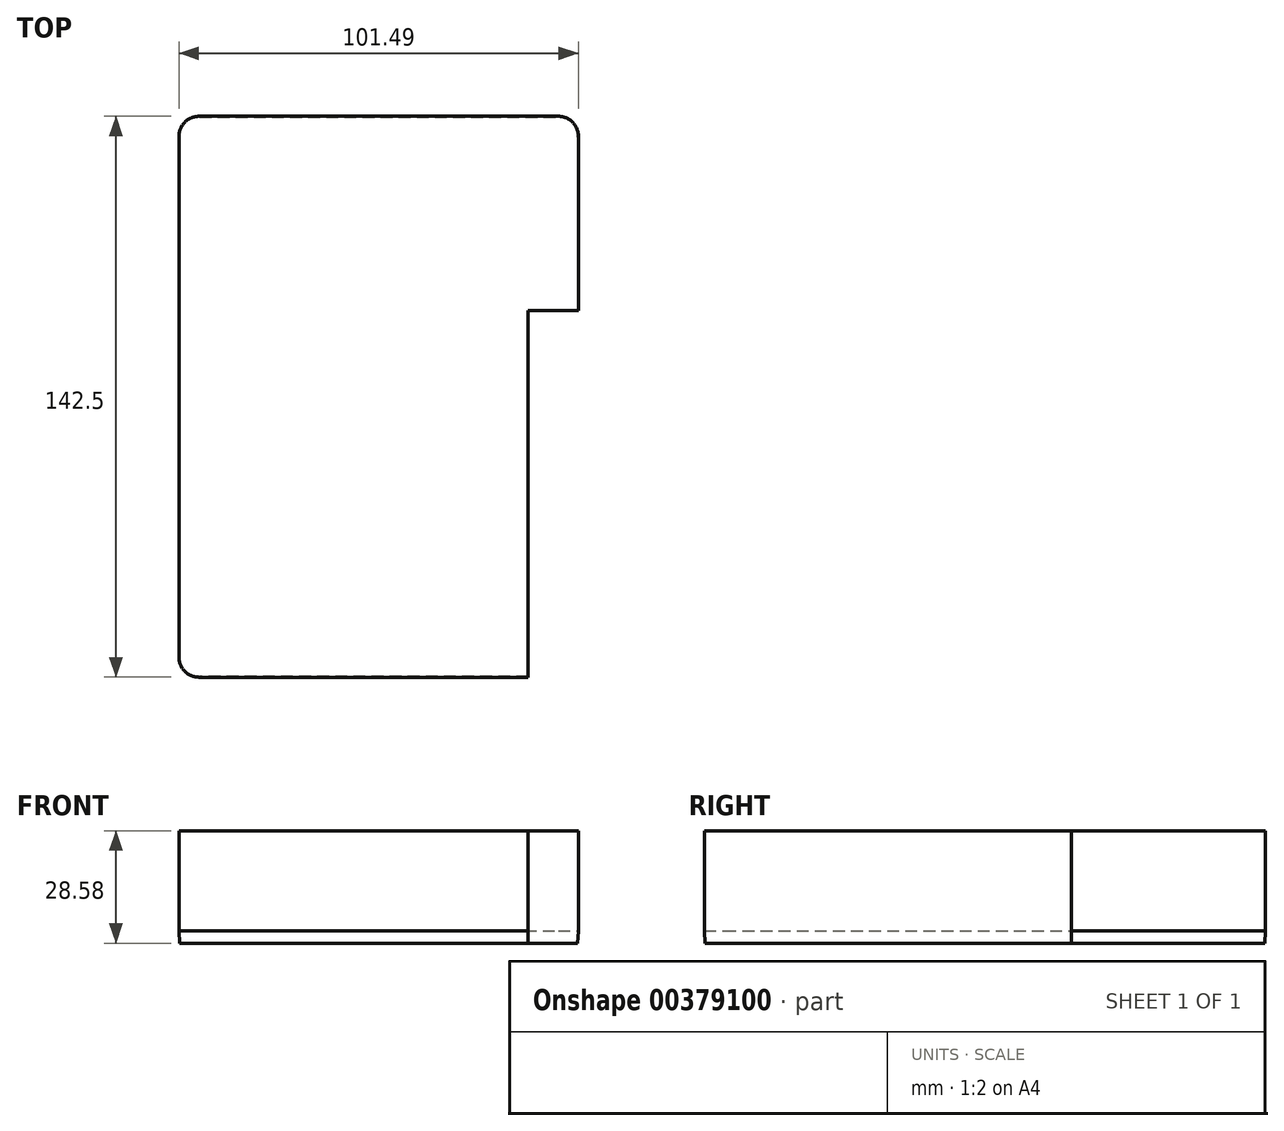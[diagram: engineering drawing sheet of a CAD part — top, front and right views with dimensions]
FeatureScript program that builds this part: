
annotation { "Feature Type Name" : "Feature", "Feature Type Description" : "" }
export const myFeature = defineFeature(function(context is Context, id is Id, definition is map)
    precondition{}
    {
        {
            var Q0;
            Q0=qCreatedBy(makeId("Top.planeOp"),FACE);
            var sketch = newSketch(context, id + "F0", { "sketchPlane" : qUnion([Q0])});
            skLineSegment(sketch, "E0.bottom", {"start": v(51.5, 49.13) * mm, "end": v(-49.64, 49.13) * mm});
            skLineSegment(sketch, "E0.top", {"start": v(51.5, -93.05) * mm, "end": v(-49.64, -93.05) * mm});
            skLineSegment(sketch, "E0.left", {"start": v(51.5, 49.13) * mm, "end": v(51.5, -93.05) * mm});
            skLineSegment(sketch, "E0.right", {"start": v(-49.64, 49.13) * mm, "end": v(-49.64, -93.05) * mm});
            skSolve(sketch);
        }
        {
            var Q0;
            Q0=makeQuery(id+"F0.imprint","IMPRINT",FACE,{"disambiguationData":[TD([[makeQuery(id+"F0.imprint","IMPRINT",EDGE,{"derivedFrom":sQuery(id+"F0.wireOp",EDGE,"E0.bottom")}),1.0]])]});
            var sketch = newSketch(context, id + "F1", { "sketchPlane" : qUnion([Q0])});
            skSolve(sketch);
        }
        {
            var Q0;
            Q0=makeQuery(id+"F1.imprint","IMPRINT",FACE,{"disambiguationData":[TD([[makeQuery(id+"F1.imprint","IMPRINT",EDGE,{"derivedFrom":makeQuery(id+"F0.imprint","IMPRINT",EDGE,{"derivedFrom":sQuery(id+"F0.wireOp",EDGE,"E0.bottom")})}),1.0]])]});
            extrude(context, id + "F2", {"entities" : qUnion([Q0]), "depth" : 3.17 * mm, "hasDraft" : true, "draftAngle" : 3 * degree});
        }
        {
            var Q0;
            Q0=makeQuery(id+"F2.opExtrude","SWEPT_EDGE",EDGE,{"disambiguationData":[OSD([sQuery(id+"F0.wireOp",EDGE,"E0.bottom"),sQuery(id+"F0.wireOp",EDGE,"E0.left")])]});
            fillet(context, id + "F3", {"entities" : qUnion([Q0]), "radius" : 5.08 * mm, "tangentPropagation" : true, "allowEdgeOverflow" : false});
        }
        {
            var Q0;
            Q0=makeQuery(id+"F2.opExtrude","SWEPT_EDGE",EDGE,{"disambiguationData":[OSD([sQuery(id+"F0.wireOp",EDGE,"E0.bottom"),sQuery(id+"F0.wireOp",EDGE,"E0.right")])]});
            fillet(context, id + "F4", {"entities" : qUnion([Q0]), "radius" : 5.08 * mm, "tangentPropagation" : true, "allowEdgeOverflow" : false});
        }
        {
            var Q0;
            Q0=makeQuery(id+"F2.opExtrude","SWEPT_EDGE",EDGE,{"disambiguationData":[OSD([sQuery(id+"F0.wireOp",EDGE,"E0.top"),sQuery(id+"F0.wireOp",EDGE,"E0.right")])]});
            fillet(context, id + "F5", {"entities" : qUnion([Q0]), "radius" : 5.08 * mm, "tangentPropagation" : true, "allowEdgeOverflow" : false});
        }
        {
            var Q0;
            Q0=makeQuery(id+"F2.opExtrude","SWEPT_EDGE",EDGE,{"disambiguationData":[OSD([sQuery(id+"F0.wireOp",EDGE,"E0.top"),sQuery(id+"F0.wireOp",EDGE,"E0.left")])]});
            fillet(context, id + "F6", {"entities" : qUnion([Q0]), "radius" : 5.08 * mm, "tangentPropagation" : true, "allowEdgeOverflow" : false});
        }
        {
            var Q0;
            Q0=makeQuery(id+"F2.opExtrude","CAP_FACE",FACE,{"disambiguationData":[OSD([sQuery(id+"F0.wireOp",EDGE,"E0.bottom"),sQuery(id+"F0.wireOp",EDGE,"E0.top"),sQuery(id+"F0.wireOp",EDGE,"E0.left"),sQuery(id+"F0.wireOp",EDGE,"E0.right")])],"isStart":false});
            var sketch = newSketch(context, id + "F7", { "sketchPlane" : qUnion([Q0])});
            skLineSegment(sketch, "E1.bottom", {"start": v(51.68, -93.21) * mm, "end": v(38.92, -93.21) * mm});
            skLineSegment(sketch, "E1.top", {"start": v(51.68, 0) * mm, "end": v(38.92, 0) * mm});
            skLineSegment(sketch, "E1.left", {"start": v(51.68, -93.21) * mm, "end": v(51.68, 0) * mm});
            skLineSegment(sketch, "E1.right", {"start": v(38.92, -93.21) * mm, "end": v(38.92, 0) * mm});
            skSolve(sketch);
        }
        {
            var Q0;
            {var subQ4=sQuery(id+"F7.wireOp",EDGE,"E1.top");Q0=makeQuery(id+"F7.imprint","IMPRINT",FACE,{"disambiguationData":[TD([[makeQuery(id+"F7.imprint","IMPRINT",EDGE,{"derivedFrom":subQ4}),1.0]])]});}
            extrude(context, id + "F8", {"entities" : qUnion([Q0]), "operationType" : NewBodyOperationType.REMOVE, "oppositeDirection" : true, "depth" : 25.4 * mm});
        }
        {
            var Q0;
            Q0=makeQuery(id+"F2.opExtrude","CAP_FACE",FACE,{"disambiguationData":[OSD([sQuery(id+"F0.wireOp",EDGE,"E0.bottom"),sQuery(id+"F0.wireOp",EDGE,"E0.top"),sQuery(id+"F0.wireOp",EDGE,"E0.left"),sQuery(id+"F0.wireOp",EDGE,"E0.right")])],"isStart":false});
            var sketch = newSketch(context, id + "F9", { "sketchPlane" : qUnion([Q0])});
            skSolve(sketch);
        }
        {
            var Q0;
            {var subQ3=sQuery(id+"F0.wireOp",EDGE,"E0.bottom");Q0=makeQuery(id+"F9.imprint","IMPRINT",FACE,{"disambiguationData":[TD([[makeQuery(id+"F9.imprint","IMPRINT",EDGE,{"derivedFrom":makeQuery(id+"F2.opExtrude","CAP_EDGE",EDGE,{"disambiguationData":[OSD([subQ3])],"isStart":false})}),1.0]])]});}
            var sketch = newSketch(context, id + "F10", { "sketchPlane" : qUnion([Q0])});
            skSolve(sketch);
        }
        {
            var Q0;
            {var subQ3=sQuery(id+"F0.wireOp",EDGE,"E0.bottom");Q0=makeQuery(id+"F9.imprint","IMPRINT",FACE,{"disambiguationData":[TD([[makeQuery(id+"F9.imprint","IMPRINT",EDGE,{"derivedFrom":makeQuery(id+"F2.opExtrude","CAP_EDGE",EDGE,{"disambiguationData":[OSD([subQ3])],"isStart":false})}),1.0]])]});}
            var sketch = newSketch(context, id + "F11", { "sketchPlane" : qUnion([Q0])});
            skSolve(sketch);
        }
        {
            var Q0;
            {var subQ3=sQuery(id+"F0.wireOp",EDGE,"E0.bottom");Q0=makeQuery(id+"F11.imprint","IMPRINT",FACE,{"disambiguationData":[TD([[makeQuery(id+"F11.imprint","IMPRINT",EDGE,{"derivedFrom":makeQuery(id+"F9.imprint","IMPRINT",EDGE,{"derivedFrom":makeQuery(id+"F2.opExtrude","CAP_EDGE",EDGE,{"disambiguationData":[OSD([subQ3])],"isStart":false})})}),1.0]])]});}
            extrude(context, id + "F12", {"entities" : qUnion([Q0]), "operationType" : NewBodyOperationType.ADD, "depth" : 25.4 * mm});
        }
    });
